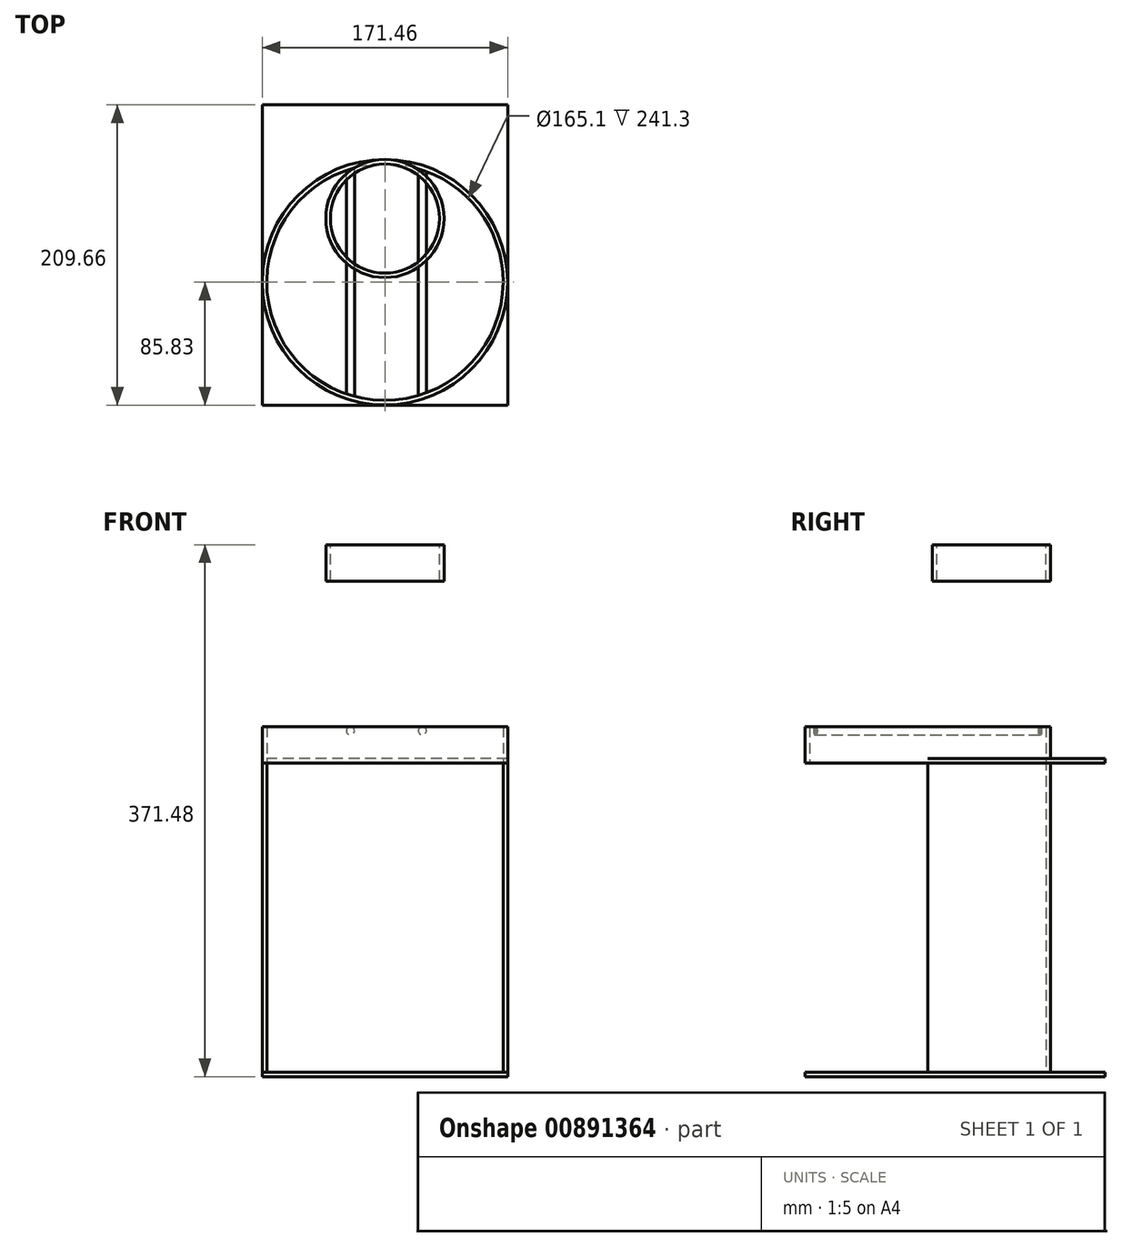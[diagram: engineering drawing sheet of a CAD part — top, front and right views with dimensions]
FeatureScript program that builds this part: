
annotation { "Feature Type Name" : "Feature", "Feature Type Description" : "" }
export const myFeature = defineFeature(function(context is Context, id is Id, definition is map)
    precondition{}
    {
        {
            var Q0;
            Q0=qCreatedBy(makeId("Top.planeOp"),FACE);
            var sketch = newSketch(context, id + "F0", { "sketchPlane" : qUnion([Q0])});
            skCircle(sketch, "E0", {"center": v(0, 0) * mm, "radius": 82.55 * mm});
            skCircle(sketch, "E1.0", {"center": v(0, 0) * mm, "radius": 85.73 * mm});
            skLineSegment(sketch, "E2", {"start": v(85.73, 0) * mm, "end": v(82.55, 0) * mm});
            skLineSegment(sketch, "E3.trimOffspring", {"start": v(-82.55, 0) * mm, "end": v(-85.73, 0) * mm});
            skSolve(sketch);
        }
        {
            var Q0;
            {var subQ0=sQuery(id+"F0.wireOp",EDGE,"E2");Q0=makeQuery(id+"F0.imprint","IMPRINT",FACE,{"disambiguationData":[TD([[makeQuery(id+"F0.imprint","IMPRINT",EDGE,{"derivedFrom":subQ0}),-1.0]])]});}
            extrude(context, id + "F1", {"entities" : qUnion([Q0]), "depth" : 215.9 * mm, "offsetDistance" : 25.4 * mm});
        }
        {
            var Q0;
            Q0=qCreatedBy(makeId("Top.planeOp"),FACE);
            var sketch = newSketch(context, id + "F2", { "sketchPlane" : qUnion([Q0])});
            skLineSegment(sketch, "E4.bottom", {"start": v(-85.73, 123.83) * mm, "end": v(85.73, 123.83) * mm});
            skLineSegment(sketch, "E4.top", {"start": v(-85.73, -123.83) * mm, "end": v(85.73, -123.83) * mm});
            skLineSegment(sketch, "E4.left", {"start": v(-85.73, 123.83) * mm, "end": v(-85.73, -123.83) * mm});
            skLineSegment(sketch, "E4.right", {"start": v(85.73, 123.83) * mm, "end": v(85.73, -123.83) * mm});
            skPoint(sketch, "E4.middle", {"position": v(0, 0) * mm});
            skSolve(sketch);
        }
        {
            var Q0;
            Q0 = qSketchRegion(id + "F2", true);
            extrude(context, id + "F3", {"entities" : qUnion([Q0]), "operationType" : NewBodyOperationType.ADD, "oppositeDirection" : true, "depth" : 3.17 * mm, "offsetDistance" : 25.4 * mm});
        }
        {
            var Q0;
            {var subQ0=sQuery(id+"F2.wireOp",EDGE,"E4.right");var subQ1=sQuery(id+"F2.wireOp",EDGE,"E4.left");var subQ2=sQuery(id+"F2.wireOp",EDGE,"E4.top");var subQ3=makeQuery(id+"F3.opExtrude","CAP_FACE",FACE,{"disambiguationData":[OSD([sQuery(id+"F2.wireOp",EDGE,"E4.bottom"),subQ2,subQ1,subQ0])],"isStart":true});Q0=makeQuery(id+"F3.boolean.opBoolean","SPLIT",FACE,{"disambiguationData":[TD([makeQuery(id+"F1.opExtrude","SWEPT_FACE",FACE,{"disambiguationData":[OSD([sQuery(id+"F0.wireOp",EDGE,"E0")])]})])],"derivedFrom":subQ3});}
            var sketch = newSketch(context, id + "F4", { "sketchPlane" : qUnion([Q0])});
            skLineSegment(sketch, "E5.bottom", {"start": v(-85.73, -123.83) * mm, "end": v(85.73, -123.83) * mm});
            skLineSegment(sketch, "E5.top", {"start": v(-85.73, -85.83) * mm, "end": v(85.73, -85.83) * mm});
            skLineSegment(sketch, "E5.left", {"start": v(-85.73, -123.83) * mm, "end": v(-85.73, -85.83) * mm});
            skLineSegment(sketch, "E5.right", {"start": v(85.73, -123.83) * mm, "end": v(85.73, -85.83) * mm});
            skSolve(sketch);
        }
        {
            var Q0;
            Q0 = qSketchRegion(id + "F4", true);
            extrude(context, id + "F5", {"entities" : qUnion([Q0]), "operationType" : NewBodyOperationType.REMOVE, "oppositeDirection" : true, "depth" : 25.4 * mm, "offsetDistance" : 25.4 * mm});
        }
        {
            var Q0;
            {var subQ0=sQuery(id+"F2.wireOp",EDGE,"E4.right");var subQ1=sQuery(id+"F2.wireOp",EDGE,"E4.left");var subQ2=sQuery(id+"F2.wireOp",EDGE,"E4.top");var subQ3=makeQuery(id+"F3.opExtrude","CAP_FACE",FACE,{"disambiguationData":[OSD([sQuery(id+"F2.wireOp",EDGE,"E4.bottom"),subQ2,subQ1,subQ0])],"isStart":true});Q0=makeQuery(id+"F3.boolean.opBoolean","SPLIT",FACE,{"disambiguationData":[TD([makeQuery(id+"F1.opExtrude","SWEPT_FACE",FACE,{"disambiguationData":[OSD([sQuery(id+"F0.wireOp",EDGE,"E0")])]})])],"derivedFrom":subQ3});}
            cPlane(context, id + "F6", {"entities" : qUnion([Q0]), "cplaneType" : CPlaneType.OFFSET, "offset" : 215.9 * mm, "width" : 152.4 * mm, "height" : 152.4 * mm});
        }
        {
            var Q0;
            Q0=qCreatedBy(id+"F6.planeOp",FACE);
            var sketch = newSketch(context, id + "F7", { "sketchPlane" : qUnion([Q0])});
            skCircle(sketch, "E6", {"center": v(0, 0) * mm, "radius": 82.55 * mm});
            skCircle(sketch, "E7.0", {"center": v(0, 0) * mm, "radius": 85.73 * mm});
            skSolve(sketch);
        }
        {
            var Q0;
            Q0=qCreatedBy(id+"F6.planeOp",FACE);
            cPlane(context, id + "F8", {"entities" : qUnion([Q0]), "cplaneType" : CPlaneType.OFFSET, "offset" : 152.4 * mm, "width" : 152.4 * mm, "height" : 152.4 * mm});
        }
        {
            var Q0;
            Q0=makeQuery(id+"F7.imprint","IMPRINT",FACE,{"disambiguationData":[TD([[makeQuery(id+"F7.imprint","IMPRINT",EDGE,{"derivedFrom":sQuery(id+"F7.wireOp",EDGE,"E6")}),-1.0]])]});
            extrude(context, id + "F9", {"entities" : qUnion([Q0]), "operationType" : NewBodyOperationType.ADD, "depth" : 25.4 * mm, "offsetDistance" : 25.4 * mm});
        }
        {
            var Q0;
            Q0=qCreatedBy(id+"F8.planeOp",FACE);
            var sketch = newSketch(context, id + "F10", { "sketchPlane" : qUnion([Q0])});
            skCircle(sketch, "E8", {"center": v(0, 44.45) * mm, "radius": 38.1 * mm});
            skCircle(sketch, "E9.0", {"center": v(0, 44.45) * mm, "radius": 41.27 * mm});
            skSolve(sketch);
        }
        {
            var Q0;
            Q0=makeQuery(id+"F10.imprint","IMPRINT",FACE,{"disambiguationData":[TD([[makeQuery(id+"F10.imprint","IMPRINT",EDGE,{"derivedFrom":sQuery(id+"F10.wireOp",EDGE,"E8")}),-1.0]])]});
            extrude(context, id + "F11", {"entities" : qUnion([Q0]), "oppositeDirection" : true, "depth" : 25.4 * mm, "offsetDistance" : 25.4 * mm});
        }
        {
            var Q0;
            Q0=qCreatedBy(id+"F6.planeOp",FACE);
            var sketch = newSketch(context, id + "F12", { "sketchPlane" : qUnion([Q0])});
            skArc(sketch, "E10.0.0", {"start": v(-85.73, 0) * mm, "mid": v(0, 85.73) * mm, "end": v(85.73, 0) * mm});
            skLineSegment(sketch, "E10.0.1", {"start": v(85.73, 0) * mm, "end": v(85.73, 123.83) * mm});
            skLineSegment(sketch, "E10.0.2", {"start": v(85.73, 123.83) * mm, "end": v(-85.73, 123.83) * mm});
            skLineSegment(sketch, "E10.0.3", {"start": v(-85.73, 123.83) * mm, "end": v(-85.73, 0) * mm});
            skSolve(sketch);
        }
        {
            var Q0;
            Q0 = qSketchRegion(id + "F12", true);
            extrude(context, id + "F13", {"entities" : qUnion([Q0]), "operationType" : NewBodyOperationType.ADD, "depth" : 3.17 * mm, "offsetDistance" : 25.4 * mm});
        }
        {
            var Q0;
            Q0=qCreatedBy(makeId("Front.planeOp"),FACE);
            var sketch = newSketch(context, id + "F14", { "sketchPlane" : qUnion([Q0])});
            skCircle(sketch, "E11", {"center": v(-24.1, 238.42) * mm, "radius": 2.83 * mm});
            skCircle(sketch, "E12", {"center": v(26.17, 238.25) * mm, "radius": 2.84 * mm});
            skSolve(sketch);
        }
        {
            var Q0;
            Q0 = qSketchRegion(id + "F14", true);
            extrude(context, id + "F15", {"entities" : qUnion([Q0]), "operationType" : NewBodyOperationType.ADD, "endBound" : BoundingType.UP_TO_NEXT, "depth" : 25.4 * mm, "offsetDistance" : 25.4 * mm, "hasSecondDirection" : true, "secondDirectionBound" : SecondDirectionBoundingType.UP_TO_NEXT, "secondDirectionOppositeDirection" : true, "secondDirectionDepth" : 25.4 * mm});
        }
    });
